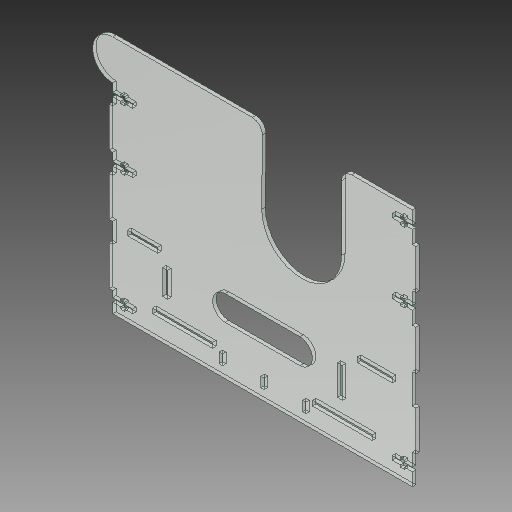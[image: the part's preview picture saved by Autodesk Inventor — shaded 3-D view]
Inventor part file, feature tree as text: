
AUTODESK INVENTOR PART (.ipt)
format: ipt  version: 2019 (Build 230136000, 136)  size: 436,224 bytes
history: native  units: mm
features: extrude x4, sketch x4, projected_geometry x2, fillet x1
ambient origin geometry x8: Origin, YZ Plane, XZ Plane, XY Plane, X Axis, Y Axis, Z Axis, Center Point
bodies: Solid1 (feature_tree)
feature tree (11):
  extrude  "Extrusion1"  Depth=220.0mm
  fillet  "Fillet1"  Radius=80.0mm
  extrude  "Extrusion3"  Depth=45.0mm
  extrude  "Extrusion4"  Depth=10.0mm
  extrude  "Extrusion5"  Depth=20.0mm
  sketch  "Sketch1"  dims[d0=300.0mm d1=220.0mm d2=80.0mm]
  sketch  "Sketch3"  dims[d3=240.0mm d6=45.0mm]
  projected_geometry  "Projected Loop1"
  sketch  "Sketch4"  dims[d7=3.5mm d8=0.0mm d20=10.0mm]
  projected_geometry  "Projected Loop2"
  sketch  "Sketch5"  dims[d21=40.0mm d22=20.0mm d23=15.0mm d24=3.5mm d25=40.0mm d26=3.5mm d27=40.0mm d28=20.0mm d29=20.0mm d30=3.5mm d31=40.0mm d32=20.0mm d35=3.5mm d36=40.0mm d37=3.5mm d38=40.0mm d39=3.5mm d40=40.0mm d41=30.0mm d42=30.0mm d43=30.0mm d44=3.5mm d45=0.0mm d46=20.0mm d47=4.0mm d48=4.0mm d49=8.0mm d50=8.0mm d51=8.0mm d52=20.0mm d53=4.0mm d54=4.0mm d55=8.0mm d56=8.0mm d57=20.0mm d58=4.0mm d59=4.0mm d60=8.0mm d61=8.0mm d62=8.0mm d63=6.0mm d65=20.0mm d66=8.0mm d67=4.0mm d68=8.0mm d69=13.0mm d70=2.0mm d71=8.0mm d72=4.0mm d73=2.0mm d74=8.0mm d75=4.0mm d76=2.0mm d77=13.0mm d78=13.0mm d79=8.0mm d80=8.0mm d81=3.5mm d82=0.0mm d84=40.0mm d85=3.5mm d86=0.0mm]
